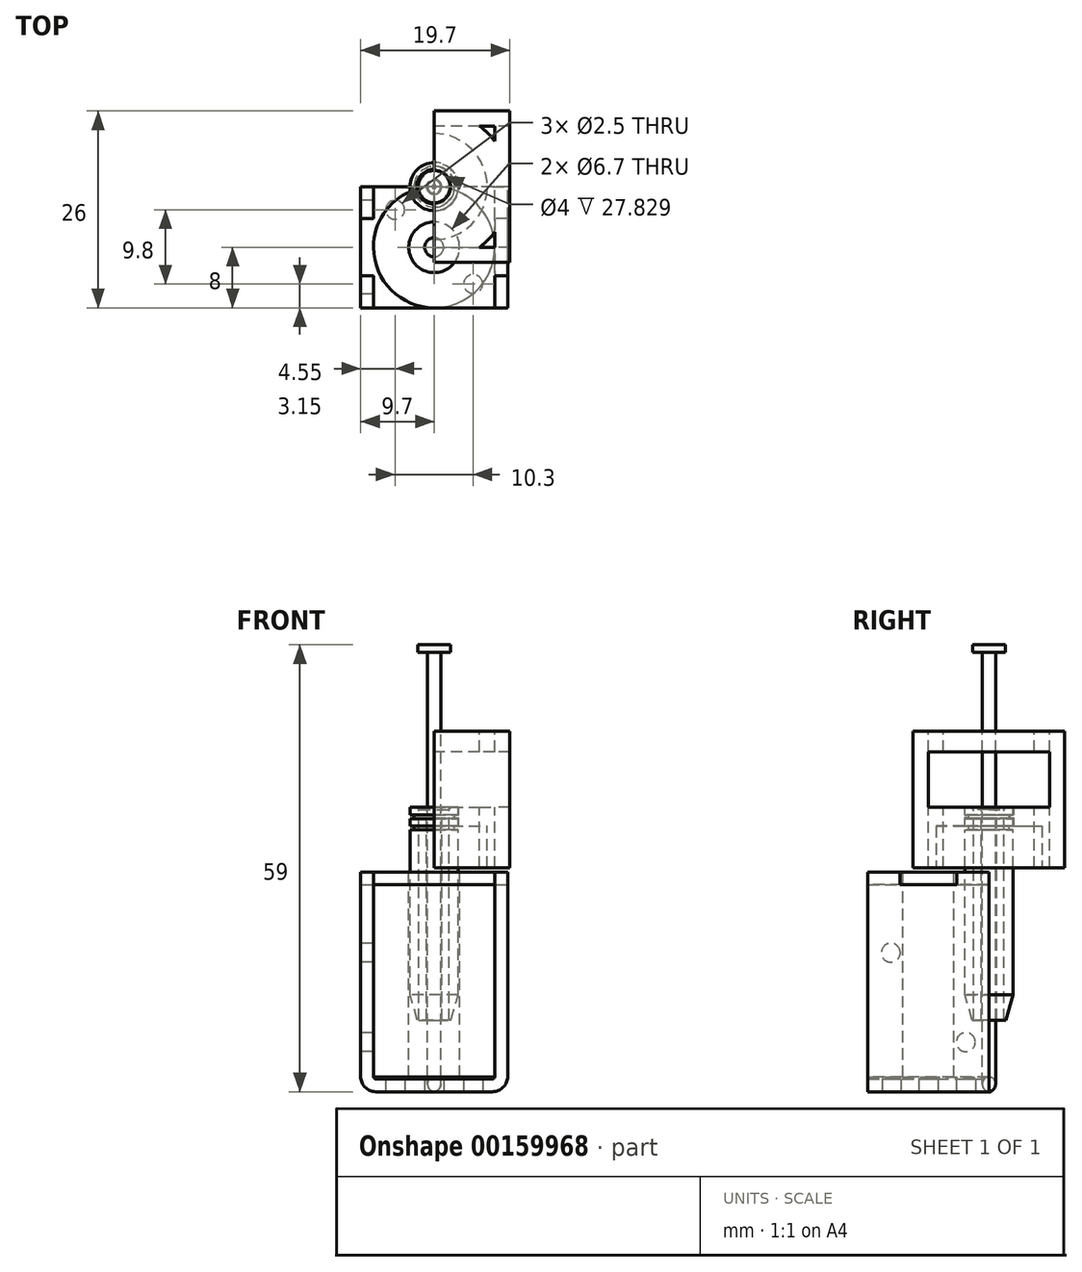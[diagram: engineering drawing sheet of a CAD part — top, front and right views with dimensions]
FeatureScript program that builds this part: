
annotation { "Feature Type Name" : "Feature", "Feature Type Description" : "" }
export const myFeature = defineFeature(function(context is Context, id is Id, definition is map)
    precondition{}
    {
        {
            var Q0;
            Q0=qCreatedBy(makeId("Front.planeOp"),FACE);
            var sketch = newSketch(context, id + "F0", { "sketchPlane" : qUnion([Q0])});
            skLineSegment(sketch, "E0", {"start": v(-9.7, 29) * mm, "end": v(-9.7, 2) * mm});
            skLineSegment(sketch, "E1", {"start": v(-7.7, 0) * mm, "end": v(7.7, 0) * mm});
            skLineSegment(sketch, "E2", {"start": v(9.7, 2) * mm, "end": v(9.7, 29) * mm});
            skLineSegment(sketch, "E3", {"start": v(9.7, 29) * mm, "end": v(8, 29) * mm});
            skLineSegment(sketch, "E4", {"start": v(8, 29) * mm, "end": v(8, 2) * mm});
            skLineSegment(sketch, "E5", {"start": v(7.7, 1.7) * mm, "end": v(-7.7, 1.7) * mm});
            skLineSegment(sketch, "E6", {"start": v(-8, 2) * mm, "end": v(-8, 29) * mm});
            skLineSegment(sketch, "E7", {"start": v(-8, 29) * mm, "end": v(-9.7, 29) * mm});
            skPoint(sketch, "E8", {"position": v(0, 0) * mm});
            skPoint(sketch, "E9.visualSharp", {"position": v(-9.7, 0) * mm});
            skArc(sketch, "E9.filletArc", {"start": v(-9.7, 2) * mm, "mid": v(-9.11, 0.59) * mm, "end": v(-7.7, 0) * mm});
            skPoint(sketch, "E10.visualSharp", {"position": v(-8, 1.7) * mm});
            skArc(sketch, "E10.filletArc", {"start": v(-8, 2) * mm, "mid": v(-7.91, 1.79) * mm, "end": v(-7.7, 1.7) * mm});
            skPoint(sketch, "E11.visualSharp", {"position": v(8, 1.7) * mm});
            skArc(sketch, "E11.filletArc", {"start": v(7.7, 1.7) * mm, "mid": v(7.91, 1.79) * mm, "end": v(8, 2) * mm});
            skPoint(sketch, "E12.visualSharp", {"position": v(9.7, 0) * mm});
            skArc(sketch, "E12.filletArc", {"start": v(7.7, 0) * mm, "mid": v(9.11, 0.59) * mm, "end": v(9.7, 2) * mm});
            skSolve(sketch);
        }
        {
            var Q0;
            Q0 = qSketchRegion(id + "F0", true);
            extrude(context, id + "F1", {"entities" : qUnion([Q0]), "depth" : 16 * mm});
        }
        {
            var Q0;
            Q0=makeQuery(id+"F1.opExtrude","SWEPT_FACE",FACE,{"disambiguationData":[OSD([sQuery(id+"F0.wireOp",EDGE,"E7")])]});
            var sketch = newSketch(context, id + "F2", { "sketchPlane" : qUnion([Q0])});
            skLineSegment(sketch, "E13", {"start": v(-8, 0) * mm, "end": v(-8, -4.23) * mm});
            skLineSegment(sketch, "E14", {"start": v(-8, -4.23) * mm, "end": v(-9.7, -4.23) * mm});
            skLineSegment(sketch, "E15", {"start": v(-9.7, -4.23) * mm, "end": v(-9.7, -11.77) * mm});
            skLineSegment(sketch, "E16", {"start": v(-9.7, -11.77) * mm, "end": v(-8, -11.77) * mm});
            skLineSegment(sketch, "E17", {"start": v(-8, -11.77) * mm, "end": v(-8, -16) * mm});
            skLineSegment(sketch, "E18.0", {"start": v(9.7, -16) * mm, "end": v(8, -16) * mm, "construction": true});
            skLineSegment(sketch, "E19", {"start": v(-8, -16) * mm, "end": v(8, -16) * mm});
            skLineSegment(sketch, "E20", {"start": v(8, -16) * mm, "end": v(8, -11.77) * mm});
            skLineSegment(sketch, "E21", {"start": v(8, -11.77) * mm, "end": v(9.7, -11.77) * mm});
            skLineSegment(sketch, "E22", {"start": v(9.7, -11.77) * mm, "end": v(9.7, -4.23) * mm});
            skLineSegment(sketch, "E23", {"start": v(9.7, -4.23) * mm, "end": v(8, -4.23) * mm});
            skLineSegment(sketch, "E24", {"start": v(8, -4.23) * mm, "end": v(8, 0) * mm});
            skLineSegment(sketch, "E25", {"start": v(8, 0) * mm, "end": v(-8, 0) * mm});
            skCircle(sketch, "E26", {"center": v(0, -8) * mm, "radius": 3.35 * mm});
            skPoint(sketch, "E26.centerSnap0", {"position": v(9.7, -8) * mm});
            skSolve(sketch);
        }
        {
            var Q0;
            Q0 = qSketchRegion(id + "F2", true);
            extrude(context, id + "F3", {"entities" : qUnion([Q0]), "operationType" : NewBodyOperationType.REMOVE, "oppositeDirection" : true, "depth" : 1.66 * mm});
        }
        {
            var Q0;
            Q0 = qSketchRegion(id + "F2", true);
            extrude(context, id + "F4", {"entities" : qUnion([Q0]), "oppositeDirection" : true, "depth" : 1.66 * mm});
        }
        {
            var Q0;
            Q0=makeQuery(id+"F4.opExtrude","CAP_FACE",FACE,{"disambiguationData":[OSD([sQuery(id+"F2.wireOp",EDGE,"E13"),sQuery(id+"F2.wireOp",EDGE,"E14"),sQuery(id+"F2.wireOp",EDGE,"E15"),sQuery(id+"F2.wireOp",EDGE,"E16"),sQuery(id+"F2.wireOp",EDGE,"E17"),sQuery(id+"F2.wireOp",EDGE,"E19"),sQuery(id+"F2.wireOp",EDGE,"E20"),sQuery(id+"F2.wireOp",EDGE,"E21"),sQuery(id+"F2.wireOp",EDGE,"E22"),sQuery(id+"F2.wireOp",EDGE,"E23"),sQuery(id+"F2.wireOp",EDGE,"E24"),sQuery(id+"F2.wireOp",EDGE,"E25"),sQuery(id+"F2.wireOp",EDGE,"E26")])],"isStart":false});
            var sketch = newSketch(context, id + "F5", { "sketchPlane" : qUnion([Q0])});
            skCircle(sketch, "E27", {"center": v(0, 8) * mm, "radius": 8 * mm});
            skCircle(sketch, "E28", {"center": v(0, 8) * mm, "radius": 3.35 * mm});
            skSolve(sketch);
        }
        {
            var Q0;
            Q0 = qSketchRegion(id + "F5", true);
            extrude(context, id + "F6", {"entities" : qUnion([Q0]), "depth" : 25.4 * mm});
        }
        {
            var Q0;
            Q0=makeQuery(id+"F1.opExtrude","SWEPT_FACE",FACE,{"disambiguationData":[OSD([sQuery(id+"F0.wireOp",EDGE,"E1")])]});
            var sketch = newSketch(context, id + "F7", { "sketchPlane" : qUnion([Q0])});
            skCircle(sketch, "E29", {"center": v(0, 8) * mm, "radius": 1.25 * mm});
            skPoint(sketch, "E29.centerSnap0", {"position": v(-7.7, 8) * mm});
            skPoint(sketch, "E30", {"position": v(5.15, 12.85) * mm});
            skPoint(sketch, "E31", {"position": v(-5.15, 3.05) * mm});
            skCircle(sketch, "E32", {"center": v(5.15, 12.85) * mm, "radius": 1.25 * mm, "construction": true});
            skCircle(sketch, "E33", {"center": v(-5.15, 3.05) * mm, "radius": 1.25 * mm, "construction": true});
            skSolve(sketch);
        }
        {
            var Q0;
            Q0 = qSketchRegion(id + "F7", true);
            extrude(context, id + "F8", {"entities" : qUnion([Q0]), "operationType" : NewBodyOperationType.REMOVE, "oppositeDirection" : true, "depth" : 25 * mm});
        }
        {
            var Q0;
            Q0=sQuery(id+"F7.wireOp",VERTEX,"E31");
            var Q1;
            Q1=sQuery(id+"F7.wireOp",VERTEX,"E30");
            var Q2;
            Q2=makeQuery(id+"F1.opExtrude","SWEPT_BODY",BODY,{"disambiguationData":[OSD([sQuery(id+"F0.wireOp",EDGE,"E0"),sQuery(id+"F0.wireOp",EDGE,"E1"),sQuery(id+"F0.wireOp",EDGE,"E2"),sQuery(id+"F0.wireOp",EDGE,"E3"),sQuery(id+"F0.wireOp",EDGE,"E4"),sQuery(id+"F0.wireOp",EDGE,"E5"),sQuery(id+"F0.wireOp",EDGE,"E6"),sQuery(id+"F0.wireOp",EDGE,"E7"),sQuery(id+"F0.wireOp",EDGE,"E9.filletArc"),sQuery(id+"F0.wireOp",EDGE,"E10.filletArc"),sQuery(id+"F0.wireOp",EDGE,"E11.filletArc"),sQuery(id+"F0.wireOp",EDGE,"E12.filletArc")])]});
            hole(context, id + "F9", {"style" : HoleStyle.SIMPLE, "endStyle" : HoleEndStyle.BLIND, "standardTappedOrClearance" : lookupTablePath({ "standard" : "ISO", "size" : "2.5", "type" : "Drilled" }), "standardBlindInLast" : lookupTablePath({ "standard" : "ISO", "size" : "2.5", "type" : "Drilled" }), "holeDiameter" : 2.5 * mm, "holeDepth" : 20 * mm, "locations" : qUnion([Q0, Q1]), "scope" : qUnion([Q2])});
        }
        {
            var Q0;
            Q0=makeQuery(id+"F1.opExtrude","SWEPT_FACE",FACE,{"disambiguationData":[OSD([sQuery(id+"F0.wireOp",EDGE,"E0")])]});
            var sketch = newSketch(context, id + "F10", { "sketchPlane" : qUnion([Q0])});
            skCircle(sketch, "E34", {"center": v(12.95, 18.35) * mm, "radius": 1.25 * mm});
            skCircle(sketch, "E35", {"center": v(3.05, 6.55) * mm, "radius": 1.25 * mm});
            skSolve(sketch);
        }
        {
            var Q0;
            Q0=sQuery(id+"F10.wireOp",VERTEX,"E34.center");
            var Q1;
            Q1=sQuery(id+"F10.wireOp",VERTEX,"E35.center");
            var Q2;
            Q2=makeQuery(id+"F1.opExtrude","SWEPT_BODY",BODY,{"disambiguationData":[OSD([sQuery(id+"F0.wireOp",EDGE,"E0"),sQuery(id+"F0.wireOp",EDGE,"E1"),sQuery(id+"F0.wireOp",EDGE,"E2"),sQuery(id+"F0.wireOp",EDGE,"E3"),sQuery(id+"F0.wireOp",EDGE,"E4"),sQuery(id+"F0.wireOp",EDGE,"E5"),sQuery(id+"F0.wireOp",EDGE,"E6"),sQuery(id+"F0.wireOp",EDGE,"E7"),sQuery(id+"F0.wireOp",EDGE,"E9.filletArc"),sQuery(id+"F0.wireOp",EDGE,"E10.filletArc"),sQuery(id+"F0.wireOp",EDGE,"E11.filletArc"),sQuery(id+"F0.wireOp",EDGE,"E12.filletArc")])]});
            hole(context, id + "F11", {"style" : HoleStyle.SIMPLE, "endStyle" : HoleEndStyle.BLIND, "standardTappedOrClearance" : lookupTablePath({ "standard" : "ISO", "size" : "2.5", "type" : "Drilled" }), "standardBlindInLast" : lookupTablePath({ "standard" : "ISO", "size" : "2.5", "type" : "Drilled" }), "holeDiameter" : 2.5 * mm, "holeDepth" : 3 * mm, "locations" : qUnion([Q0, Q1]), "scope" : qUnion([Q2])});
        }
        {
            var Q0;
            Q0=qCreatedBy(makeId("Front.planeOp"),FACE);
            var sketch = newSketch(context, id + "F12", { "sketchPlane" : qUnion([Q0])});
            skLineSegment(sketch, "E36", {"start": v(3.17, 37.57) * mm, "end": v(3.17, 36.57) * mm});
            skLineSegment(sketch, "E37", {"start": v(0, 27.54) * mm, "end": v(0, -6.67) * mm, "construction": true});
            skLineSegment(sketch, "E38", {"start": v(3.17, 37.57) * mm, "end": v(2, 37.57) * mm});
            skPoint(sketch, "E39.orphan", {"position": v(0, 37.57) * mm});
            skLineSegment(sketch, "E40", {"start": v(2, 37.57) * mm, "end": v(2, 9.44) * mm});
            skLineSegment(sketch, "E41", {"start": v(3.18, 12.77) * mm, "end": v(2.2, 9.44) * mm});
            skLineSegment(sketch, "E42", {"start": v(2.2, 9.44) * mm, "end": v(2, 9.44) * mm});
            skLineSegment(sketch, "E43", {"start": v(3.17, 36.57) * mm, "end": v(2.67, 36.57) * mm});
            skLineSegment(sketch, "E44", {"start": v(2.67, 36.57) * mm, "end": v(2.67, 36.07) * mm});
            skLineSegment(sketch, "E45", {"start": v(2.67, 36.07) * mm, "end": v(3.17, 36.07) * mm});
            skLineSegment(sketch, "E46.trimOffspring", {"start": v(3.17, 36.07) * mm, "end": v(3.17, 35.07) * mm});
            skLineSegment(sketch, "E47", {"start": v(3.17, 35.07) * mm, "end": v(2.67, 35.07) * mm});
            skLineSegment(sketch, "E48", {"start": v(2.67, 35.07) * mm, "end": v(2.67, 34.57) * mm});
            skLineSegment(sketch, "E49", {"start": v(2.67, 34.57) * mm, "end": v(3.17, 34.57) * mm});
            skLineSegment(sketch, "E50.trimOffspring", {"start": v(3.17, 34.57) * mm, "end": v(3.17, 12.77) * mm});
            skSolve(sketch);
        }
        {
            var Q0;
            Q0 = qSketchRegion(id + "F12", true);
            var Q1;
            Q1=sQuery(id+"F12.wireOp",EDGE,"E37");
            revolve(context, id + "F13", {"entities" : qUnion([Q0]), "axis" : qUnion([Q1]), "revolveType" : RevolveType.FULL});
        }
        {
            var Q0;
            Q0=makeQuery(id+"F13.opRevolve","SWEPT_EDGE",EDGE,{"disambiguationData":[OSD([sQuery(id+"F12.wireOp",EDGE,"E38"),sQuery(id+"F12.wireOp",EDGE,"E40")])]});
            chamfer(context, id + "F14", {"entities" : qUnion([Q0]), "width" : 0.3 * mm, "tangentPropagation" : true});
        }
        {
            var Q0;
            Q0=makeQuery(id+"F13.opRevolve","SWEPT_FACE",FACE,{"disambiguationData":[OSD([sQuery(id+"F12.wireOp",EDGE,"E38")])]});
            var sketch = newSketch(context, id + "F15", { "sketchPlane" : qUnion([Q0])});
            skCircle(sketch, "E51", {"center": v(0, 0) * mm, "radius": 2 * mm});
            skCircle(sketch, "E52", {"center": v(0, 0) * mm, "radius": 1 * mm});
            skSolve(sketch);
        }
        {
            var Q0;
            Q0 = qSketchRegion(id + "F15", true);
            var Q1;
            Q1=makeQuery(id+"F13.opRevolve","SWEPT_FACE",FACE,{"disambiguationData":[OSD([sQuery(id+"F12.wireOp",EDGE,"E42")])]});
            extrude(context, id + "F16", {"entities" : qUnion([Q0]), "endBound" : BoundingType.UP_TO_SURFACE, "oppositeDirection" : true, "endBoundEntityFace" : qUnion([Q1]), "depth" : 25 * mm});
        }
        {
            var Q0;
            Q0=qCreatedBy(makeId("Front.planeOp"),FACE);
            var sketch = newSketch(context, id + "F17", { "sketchPlane" : qUnion([Q0])});
            skLineSegment(sketch, "E53", {"start": v(10, 29.58) * mm, "end": v(10, 47.61) * mm});
            skLineSegment(sketch, "E54", {"start": v(10, 47.61) * mm, "end": v(0, 47.61) * mm});
            skLineSegment(sketch, "E55", {"start": v(0, 47.61) * mm, "end": v(0, 44.87) * mm});
            skLineSegment(sketch, "E56", {"start": v(0, 44.87) * mm, "end": v(8.8, 44.87) * mm});
            skLineSegment(sketch, "E57", {"start": v(8.8, 44.87) * mm, "end": v(8.8, 37.57) * mm});
            skLineSegment(sketch, "E58", {"start": v(8.8, 37.57) * mm, "end": v(3.23, 37.57) * mm});
            skLineSegment(sketch, "E59", {"start": v(3.23, 37.57) * mm, "end": v(3.23, 36.57) * mm});
            skLineSegment(sketch, "E60", {"start": v(3.23, 36.57) * mm, "end": v(2.73, 36.57) * mm});
            skLineSegment(sketch, "E61", {"start": v(2.73, 36.57) * mm, "end": v(2.73, 36.17) * mm});
            skLineSegment(sketch, "E62", {"start": v(2.73, 36.17) * mm, "end": v(3.23, 36.17) * mm});
            skLineSegment(sketch, "E63", {"start": v(3.23, 36.17) * mm, "end": v(3.23, 35.1) * mm});
            skLineSegment(sketch, "E64", {"start": v(3.23, 35.1) * mm, "end": v(7, 35.1) * mm});
            skLineSegment(sketch, "E65", {"start": v(7, 35.1) * mm, "end": v(7, 29.58) * mm});
            skLineSegment(sketch, "E66", {"start": v(7, 29.58) * mm, "end": v(10, 29.58) * mm});
            skSolve(sketch);
        }
        {
            var Q0;
            Q0 = qSketchRegion(id + "F17", true);
            var Q1;
            Q1=sQuery(id+"F17.wireOp",EDGE,"E55");
            revolve(context, id + "F18", {"entities" : qUnion([Q0]), "axis" : qUnion([Q1]), "revolveType" : RevolveType.SYMMETRIC, "angle" : 180 * degree});
        }
        {
            var Q0;
            Q0=makeQuery(id+"F18.opRevolve","SWEPT_FACE",FACE,{"disambiguationData":[OSD([sQuery(id+"F17.wireOp",EDGE,"E54")])]});
            var sketch = newSketch(context, id + "F19", { "sketchPlane" : qUnion([Q0])});
            skPoint(sketch, "E67.oppositeSnap0", {"position": v(10, 0) * mm});
            skLineSegment(sketch, "E67.bottom", {"start": v(0, -10) * mm, "end": v(10, -10) * mm});
            skLineSegment(sketch, "E67.top", {"start": v(0, 10) * mm, "end": v(10, 10) * mm});
            skLineSegment(sketch, "E67.right", {"start": v(10, -10) * mm, "end": v(10, 10) * mm});
            skLineSegment(sketch, "E68", {"start": v(0, -10) * mm, "end": v(0, -8) * mm});
            skLineSegment(sketch, "E69", {"start": v(0, -8) * mm, "end": v(8, -8) * mm});
            skLineSegment(sketch, "E70", {"start": v(8, -8) * mm, "end": v(8, 8) * mm});
            skLineSegment(sketch, "E71", {"start": v(8, 8) * mm, "end": v(0, 8) * mm});
            skLineSegment(sketch, "E72", {"start": v(0, 8) * mm, "end": v(0, 10) * mm});
            skSolve(sketch);
        }
        {
            var Q0;
            Q0 = qSketchRegion(id + "F19", true);
            var Q1;
            Q1=makeQuery(id+"F18.opRevolve","SWEPT_FACE",FACE,{"disambiguationData":[OSD([sQuery(id+"F17.wireOp",EDGE,"E66")])]});
            extrude(context, id + "F20", {"entities" : qUnion([Q0]), "operationType" : NewBodyOperationType.ADD, "endBound" : BoundingType.UP_TO_SURFACE, "oppositeDirection" : true, "endBoundEntityFace" : qUnion([Q1]), "depth" : 25 * mm});
        }
        {
            var Q0;
            Q0=makeQuery(id+"F20.boolean.opBoolean","MERGE",FACE,{"derivedFrom":[makeQuery(id+"F18.opRevolve","CAP_FACE",FACE,{"disambiguationData":[OSD([sQuery(id+"F17.wireOp",EDGE,"E53"),sQuery(id+"F17.wireOp",EDGE,"E54"),sQuery(id+"F17.wireOp",EDGE,"E55"),sQuery(id+"F17.wireOp",EDGE,"E56"),sQuery(id+"F17.wireOp",EDGE,"E57"),sQuery(id+"F17.wireOp",EDGE,"E58"),sQuery(id+"F17.wireOp",EDGE,"E59"),sQuery(id+"F17.wireOp",EDGE,"E60"),sQuery(id+"F17.wireOp",EDGE,"E61"),sQuery(id+"F17.wireOp",EDGE,"E62"),sQuery(id+"F17.wireOp",EDGE,"E63"),sQuery(id+"F17.wireOp",EDGE,"E64"),sQuery(id+"F17.wireOp",EDGE,"E65"),sQuery(id+"F17.wireOp",EDGE,"E66")])],"isStart":false}),makeQuery(id+"F20.opExtrude","SWEPT_FACE",FACE,{"disambiguationData":[OSD([sQuery(id+"F19.wireOp",EDGE,"E68")])]}),makeQuery(id+"F20.opExtrude","SWEPT_FACE",FACE,{"disambiguationData":[OSD([sQuery(id+"F19.wireOp",EDGE,"E72")])]})]});
            var sketch = newSketch(context, id + "F21", { "sketchPlane" : qUnion([Q0])});
            skLineSegment(sketch, "E73.bottom", {"start": v(8, 44.87) * mm, "end": v(-8, 44.87) * mm});
            skLineSegment(sketch, "E73.top", {"start": v(8, 37.57) * mm, "end": v(-8, 37.57) * mm});
            skLineSegment(sketch, "E73.left", {"start": v(8, 44.87) * mm, "end": v(8, 37.57) * mm});
            skLineSegment(sketch, "E73.right", {"start": v(-8, 44.87) * mm, "end": v(-8, 37.57) * mm});
            skSolve(sketch);
        }
        {
            var Q0;
            Q0=makeQuery(id+"F21.imprint","IMPRINT",FACE,{"disambiguationData":[TD([[makeQuery(id+"F21.imprint","IMPRINT",EDGE,{"derivedFrom":sQuery(id+"F21.wireOp",EDGE,"E73.bottom")}),-1.0]])]});
            extrude(context, id + "F22", {"entities" : qUnion([Q0]), "operationType" : NewBodyOperationType.REMOVE, "oppositeDirection" : true, "depth" : 25 * mm});
        }
        {
            var Q0;
            Q0=qCreatedBy(makeId("Right.planeOp"),FACE);
            var sketch = newSketch(context, id + "F23", { "sketchPlane" : qUnion([Q0])});
            skLineSegment(sketch, "E74", {"start": v(0.13, 0) * mm, "end": v(0, 0) * mm});
            skLineSegment(sketch, "E75", {"start": v(-0.87, 1) * mm, "end": v(-0.88, 58) * mm});
            skLineSegment(sketch, "E76", {"start": v(-0.88, 58) * mm, "end": v(-2.15, 58) * mm});
            skLineSegment(sketch, "E77", {"start": v(-2.15, 58) * mm, "end": v(-2.15, 59) * mm});
            skLineSegment(sketch, "E78", {"start": v(-2.15, 59) * mm, "end": v(0, 59) * mm});
            skLineSegment(sketch, "E79", {"start": v(0, 59) * mm, "end": v(0, 0) * mm});
            skPoint(sketch, "E80.visualSharp", {"position": v(-0.87, 0) * mm});
            skArc(sketch, "E80.filletArc", {"start": v(-0.87, 1) * mm, "mid": v(-0.58, 0.3) * mm, "end": v(0.13, 0) * mm});
            skLineSegment(sketch, "E81", {"start": v(0, 0) * mm, "end": v(0, -9.54) * mm, "construction": true});
            skSolve(sketch);
        }
        {
            var Q0;
            Q0 = qSketchRegion(id + "F23", true);
            var Q1;
            Q1=sQuery(id+"F23.wireOp",EDGE,"E79");
            revolve(context, id + "F24", {"entities" : qUnion([Q0]), "axis" : qUnion([Q1]), "revolveType" : RevolveType.FULL});
        }
    });
